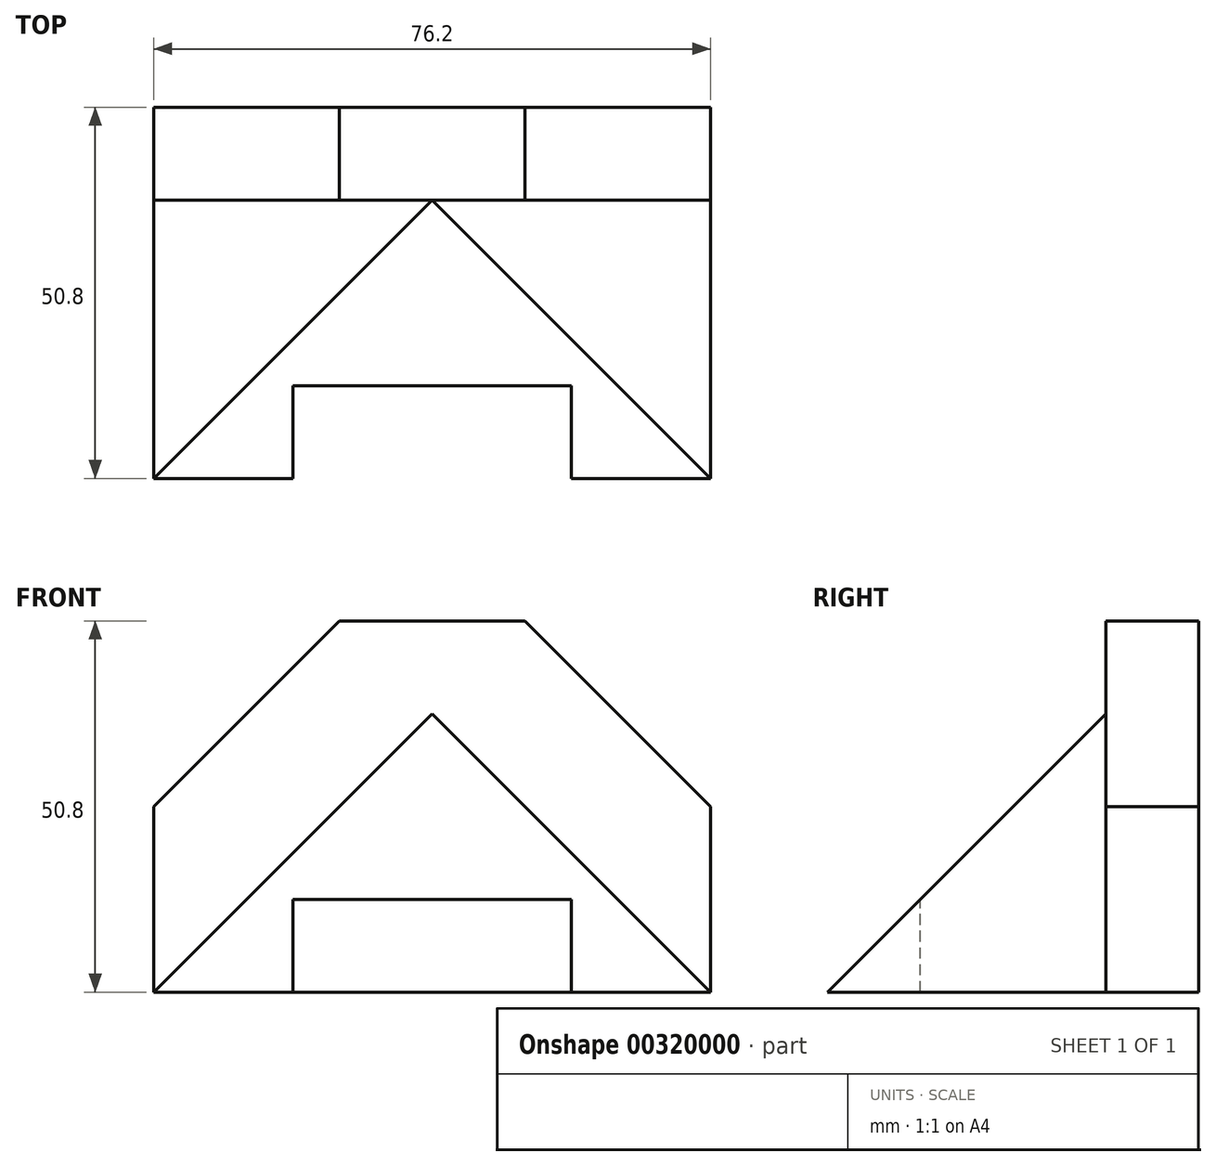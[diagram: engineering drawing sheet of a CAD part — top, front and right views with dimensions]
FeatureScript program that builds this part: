
annotation { "Feature Type Name" : "Feature", "Feature Type Description" : "" }
export const myFeature = defineFeature(function(context is Context, id is Id, definition is map)
    precondition{}
    {
        {
            var Q0;
            Q0=qCreatedBy(makeId("Front.planeOp"),FACE);
            var sketch = newSketch(context, id + "F0", { "sketchPlane" : qUnion([Q0])});
            skLineSegment(sketch, "E0", {"start": v(76.2, 0) * mm, "end": v(0, 0) * mm});
            skLineSegment(sketch, "E1", {"start": v(0, 0) * mm, "end": v(0, 25.4) * mm});
            skLineSegment(sketch, "E2", {"start": v(0, 25.4) * mm, "end": v(25.4, 50.8) * mm});
            skLineSegment(sketch, "E3", {"start": v(25.4, 50.8) * mm, "end": v(50.8, 50.8) * mm});
            skLineSegment(sketch, "E4", {"start": v(50.8, 50.8) * mm, "end": v(76.2, 25.4) * mm});
            skLineSegment(sketch, "E5", {"start": v(76.2, 25.4) * mm, "end": v(76.2, 0) * mm});
            skSolve(sketch);
        }
        {
            var Q0;
            Q0 = qSketchRegion(id + "F0", true);
            extrude(context, id + "F1", {"entities" : qUnion([Q0]), "depth" : 50.8 * mm});
        }
        {
            var Q0;
            Q0=makeQuery(id+"F1.opExtrude","CAP_FACE",FACE,{"disambiguationData":[OSD([sQuery(id+"F0.wireOp",EDGE,"E0"),sQuery(id+"F0.wireOp",EDGE,"E1"),sQuery(id+"F0.wireOp",EDGE,"E2"),sQuery(id+"F0.wireOp",EDGE,"E3"),sQuery(id+"F0.wireOp",EDGE,"E4"),sQuery(id+"F0.wireOp",EDGE,"E5")])],"isStart":false});
            var sketch = newSketch(context, id + "F2", { "sketchPlane" : qUnion([Q0])});
            skLineSegment(sketch, "E6", {"start": v(0, 0) * mm, "end": v(38.1, 38.1) * mm});
            skLineSegment(sketch, "E7", {"start": v(38.1, 38.1) * mm, "end": v(76.2, 0) * mm});
            skLineSegment(sketch, "E8", {"start": v(19.05, 0) * mm, "end": v(19.05, 12.7) * mm});
            skLineSegment(sketch, "E9", {"start": v(19.05, 12.7) * mm, "end": v(57.15, 12.7) * mm});
            skLineSegment(sketch, "E10", {"start": v(57.15, 12.7) * mm, "end": v(57.15, 0) * mm});
            skSolve(sketch);
        }
        {
            var Q0;
            {var subQ0=sQuery(id+"F2.wireOp",EDGE,"E8");Q0=makeQuery(id+"F2.imprint","IMPRINT",FACE,{"disambiguationData":[TD([[makeQuery(id+"F2.imprint","IMPRINT",EDGE,{"derivedFrom":subQ0}),-1.0]])]});}
            extrude(context, id + "F3", {"entities" : qUnion([Q0]), "operationType" : NewBodyOperationType.REMOVE, "oppositeDirection" : true, "depth" : 12.7 * mm});
        }
        {
            var Q0;
            Q0=makeQuery(id+"F1.opExtrude","SWEPT_FACE",FACE,{"disambiguationData":[OSD([sQuery(id+"F0.wireOp",EDGE,"E5")])]});
            var sketch = newSketch(context, id + "F4", { "sketchPlane" : qUnion([Q0])});
            skLineSegment(sketch, "E11", {"start": v(-50.8, 0) * mm, "end": v(-12.7, 38.1) * mm});
            skLineSegment(sketch, "E12", {"start": v(-12.7, 38.1) * mm, "end": v(-12.7, 25.4) * mm});
            skLineSegment(sketch, "E13", {"start": v(-12.7, 25.4) * mm, "end": v(0, 25.4) * mm});
            skLineSegment(sketch, "E14", {"start": v(0, 25.4) * mm, "end": v(0, 0) * mm});
            skLineSegment(sketch, "E15", {"start": v(0, 0) * mm, "end": v(-50.8, 0) * mm});
            skLineSegment(sketch, "E16", {"start": v(-12.7, 38.1) * mm, "end": v(-12.7, 50.8) * mm});
            skLineSegment(sketch, "E17", {"start": v(-12.7, 50.8) * mm, "end": v(0, 50.8) * mm});
            skLineSegment(sketch, "E18", {"start": v(0, 50.8) * mm, "end": v(0, 0) * mm});
            skLineSegment(sketch, "E19", {"start": v(-12.7, 25.4) * mm, "end": v(-12.7, 0) * mm});
            skLineSegment(sketch, "E20", {"start": v(-12.7, 0) * mm, "end": v(0, 0) * mm});
            skLineSegment(sketch, "E21", {"start": v(-50.8, 25.4) * mm, "end": v(-25.4, 25.4) * mm});
            skLineSegment(sketch, "E22", {"start": v(-25.4, 25.4) * mm, "end": v(-12.7, 38.1) * mm});
            skLineSegment(sketch, "E23", {"start": v(-12.7, 50.8) * mm, "end": v(-50.8, 50.8) * mm});
            skLineSegment(sketch, "E24", {"start": v(-50.8, 50.8) * mm, "end": v(-50.8, 25.4) * mm});
            skSolve(sketch);
        }
        {
            var Q0;
            Q0=makeQuery(id+"F4.imprint","IMPRINT",FACE,{"disambiguationData":[TD([[makeQuery(id+"F4.imprint","IMPRINT",EDGE,{"derivedFrom":sQuery(id+"F4.wireOp",EDGE,"E16")}),1.0]])]});
            var Q1;
            Q1=makeQuery(id+"F4.imprint","IMPRINT",FACE,{"disambiguationData":[TD([[makeQuery(id+"F4.imprint","IMPRINT",EDGE,{"derivedFrom":sQuery(id+"F4.wireOp",EDGE,"E11")}),1.0]])]});
            extrude(context, id + "F5", {"entities" : qUnion([Q0, Q1]), "operationType" : NewBodyOperationType.REMOVE, "endBound" : BoundingType.THROUGH_ALL, "oppositeDirection" : true, "depth" : 25.4 * mm});
        }
        {
            var Q0;
            Q0=makeQuery(id+"F5.boolean.opBoolean","COPY",FACE,{"derivedFrom":makeQuery(id+"F5.opExtrude","SWEPT_FACE",FACE,{"disambiguationData":[OSD([sQuery(id+"F4.wireOp",EDGE,"E16")])]})});
            var sketch = newSketch(context, id + "F6", { "sketchPlane" : qUnion([Q0])});
            skLineSegment(sketch, "E25", {"start": v(38.1, 38.1) * mm, "end": v(76.2, 0) * mm});
            skLineSegment(sketch, "E26", {"start": v(76.2, 0) * mm, "end": v(76.2, 38.1) * mm});
            skLineSegment(sketch, "E27", {"start": v(76.2, 38.1) * mm, "end": v(38.1, 38.1) * mm});
            skLineSegment(sketch, "E28", {"start": v(38.1, 38.1) * mm, "end": v(0, 0) * mm});
            skLineSegment(sketch, "E29", {"start": v(0, 0) * mm, "end": v(0, 38.1) * mm});
            skLineSegment(sketch, "E30", {"start": v(0, 38.1) * mm, "end": v(38.1, 38.1) * mm});
            skSolve(sketch);
        }
        {
            var Q0;
            Q0 = qSketchRegion(id + "F6", true);
            extrude(context, id + "F7", {"entities" : qUnion([Q0]), "operationType" : NewBodyOperationType.REMOVE, "endBound" : BoundingType.THROUGH_ALL, "depth" : 25.4 * mm});
        }
    });
